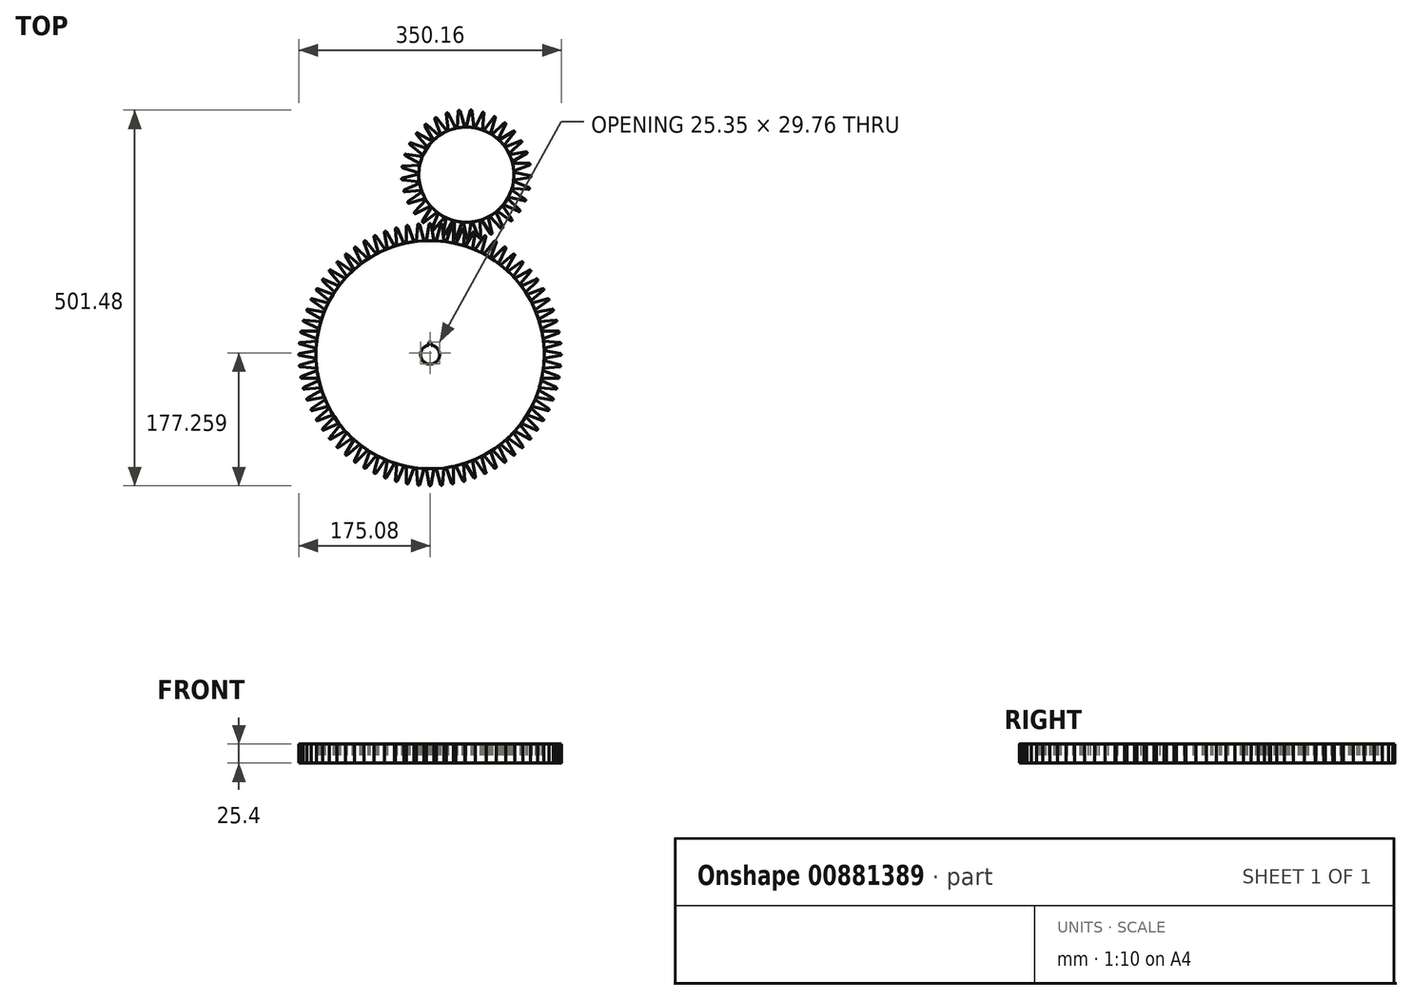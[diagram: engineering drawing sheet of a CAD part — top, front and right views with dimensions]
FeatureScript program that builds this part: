
annotation { "Feature Type Name" : "Feature", "Feature Type Description" : "" }
export const myFeature = defineFeature(function(context is Context, id is Id, definition is map)
    precondition{}
    {
        {
            var Q0;
            Q0=qCreatedBy(makeId("Top.planeOp"),FACE);
            var sketch = newSketch(context, id + "F0", { "sketchPlane" : qUnion([Q0])});
            skArc(sketch, "E0", {"start": v(21.45, 150.88) * mm, "mid": v(-26.46, -150.08) * mm, "end": v(31.45, 149.12) * mm});
            skLineSegment(sketch, "E1", {"start": v(21.45, 150.88) * mm, "end": v(31.45, 178.37) * mm});
            skLineSegment(sketch, "E2", {"start": v(31.45, 178.37) * mm, "end": v(31.45, 149.12) * mm});
            skLineSegment(sketch, "E3", {"start": v(21.45, 150.88) * mm, "end": v(31.45, 149.12) * mm});
            skArc(sketch, "E4", {"start": v(-1.59, 12.6) * mm, "mid": v(0, -12.7) * mm, "end": v(1.59, 12.6) * mm});
            skLineSegment(sketch, "E5.bottom", {"start": v(-1.59, 17.06) * mm, "end": v(1.59, 17.06) * mm});
            skLineSegment(sketch, "E5.left", {"start": v(-1.59, 17.06) * mm, "end": v(-1.59, 12.6) * mm});
            skLineSegment(sketch, "E5.right", {"start": v(1.59, 17.06) * mm, "end": v(1.59, 12.6) * mm});
            skPoint(sketch, "E5.top.end.orphan", {"position": v(1.59, -17.06) * mm});
            skPoint(sketch, "E6.orphan", {"position": v(-1.59, -17.06) * mm});
            skCircle(sketch, "E7", {"center": v(48.43, 240.28) * mm, "radius": 63.5 * mm});
            skLineSegment(sketch, "E8", {"start": v(0, 0) * mm, "end": v(2.5, 12.45) * mm, "construction": true});
            skLineSegment(sketch, "E9", {"start": v(32.72, 178.75) * mm, "end": v(32.72, 149.11) * mm});
            skLineSegment(sketch, "E10", {"start": v(32.72, 149.11) * mm, "end": v(42.74, 177.03) * mm});
            skLineSegment(sketch, "E11", {"start": v(42.74, 177.03) * mm, "end": v(32.72, 178.75) * mm});
            skSolve(sketch);
        }
        {
            var Q0;
            Q0=makeQuery(id+"F0.imprint","IMPRINT",FACE,{"disambiguationData":[TD([[makeQuery(id+"F0.imprint","IMPRINT",EDGE,{"derivedFrom":sQuery(id+"F0.wireOp",EDGE,"E0")}),1.0]])]});
            extrude(context, id + "F1", {"entities" : qUnion([Q0]), "depth" : 25.4 * mm, "offsetDistance" : 25.4 * mm});
        }
        {
            var Q0;
            Q0=makeQuery(id+"F0.imprint","IMPRINT",FACE,{"disambiguationData":[TD([[makeQuery(id+"F0.imprint","IMPRINT",EDGE,{"derivedFrom":sQuery(id+"F0.wireOp",EDGE,"E1")}),-1.0]])]});
            extrude(context, id + "F2", {"entities" : qUnion([Q0]), "depth" : 25.4 * mm, "offsetDistance" : 25.4 * mm});
        }
        {
            var Q0;
            Q0=makeQuery(id+"F2.opExtrude","SWEPT_EDGE",EDGE,{"disambiguationData":[OSD([sQuery(id+"F0.wireOp",EDGE,"E1"),sQuery(id+"F0.wireOp",EDGE,"E2")])]});
            fillet(context, id + "F3", {"entities" : qUnion([Q0]), "radius" : 1.27 * mm, "tangentPropagation" : true, "allowEdgeOverflow" : false});
        }
        {
            var Q0;
            Q0=makeQuery(id+"F2.opExtrude","SWEPT_BODY",BODY,{"disambiguationData":[OSD([sQuery(id+"F0.wireOp",EDGE,"E1"),sQuery(id+"F0.wireOp",EDGE,"E2"),sQuery(id+"F0.wireOp",EDGE,"E3")])]});
            var Q1;
            Q1=makeQuery(id+"F1.opExtrude","SWEPT_FACE",FACE,{"disambiguationData":[OSD([sQuery(id+"F0.wireOp",EDGE,"E0")])]});
            circularPattern(context, id + "F4", {"entities" : qUnion([Q0]), "axis" : qUnion([Q1]), "angle" : 360 * degree, "instanceCount" : 72, "equalSpace" : true});
        }
        {
            var Q0;
            {var subQ0=sQuery(id+"F0.wireOp",EDGE,"E11");Q0=makeQuery(id+"F0.imprint","IMPRINT",FACE,{"disambiguationData":[TD([[makeQuery(id+"F0.imprint","IMPRINT",EDGE,{"derivedFrom":subQ0}),-1.0]])]});}
            extrude(context, id + "F5", {"entities" : qUnion([Q0]), "depth" : 25.4 * mm, "offsetDistance" : 25.4 * mm});
        }
        {
            var Q0;
            {var subQ1=sQuery(id+"F0.wireOp",EDGE,"E9");Q0=makeQuery(id+"F0.imprint","IMPRINT",FACE,{"disambiguationData":[TD([[makeQuery(id+"F0.imprint","IMPRINT",EDGE,{"derivedFrom":subQ1}),1.0]])]});}
            extrude(context, id + "F6", {"entities" : qUnion([Q0]), "depth" : 25.4 * mm, "offsetDistance" : 25.4 * mm});
        }
        {
            var Q0;
            Q0=makeQuery(id+"F6.opExtrude","SWEPT_EDGE",EDGE,{"disambiguationData":[OSD([sQuery(id+"F0.wireOp",EDGE,"E9"),sQuery(id+"F0.wireOp",EDGE,"E10")])]});
            fillet(context, id + "F7", {"entities" : qUnion([Q0]), "radius" : 1.27 * mm, "tangentPropagation" : true, "allowEdgeOverflow" : false});
        }
        {
            var Q0;
            Q0=makeQuery(id+"F6.opExtrude","SWEPT_BODY",BODY,{"disambiguationData":[OSD([sQuery(id+"F0.wireOp",EDGE,"E7"),sQuery(id+"F0.wireOp",EDGE,"E9"),sQuery(id+"F0.wireOp",EDGE,"E10")])]});
            var Q1;
            Q1=makeQuery(id+"F5.opExtrude","SWEPT_FACE",FACE,{"disambiguationData":[OSD([sQuery(id+"F0.wireOp",EDGE,"E7")])]});
            circularPattern(context, id + "F8", {"entities" : qUnion([Q0]), "axis" : qUnion([Q1]), "angle" : 360 * degree, "instanceCount" : 33, "equalSpace" : true});
        }
    });
